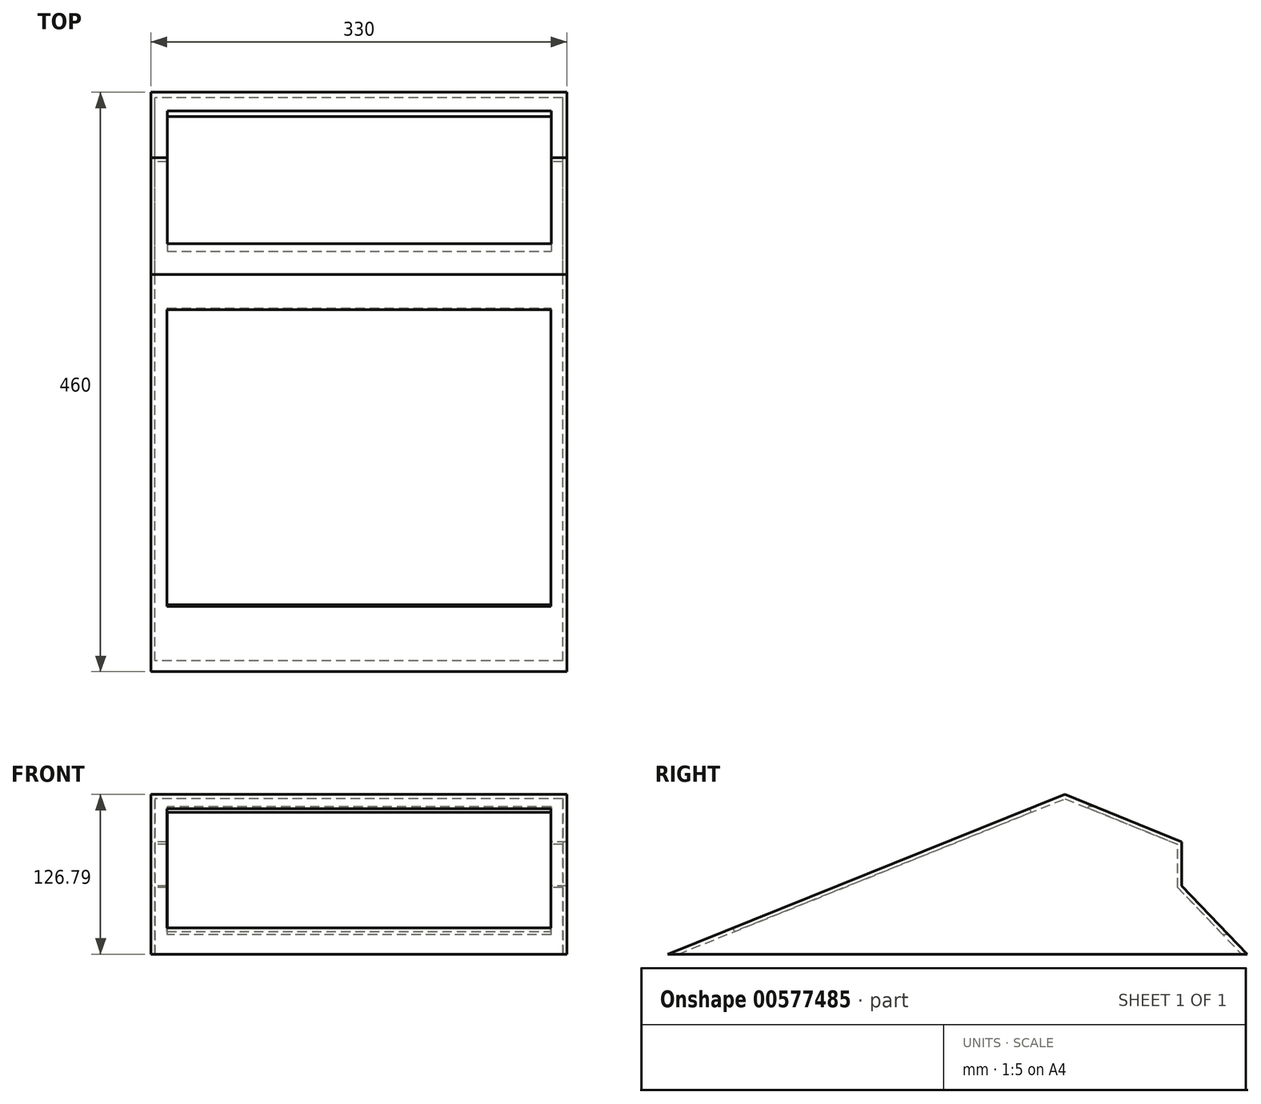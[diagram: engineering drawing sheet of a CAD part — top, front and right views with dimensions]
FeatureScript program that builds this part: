
annotation { "Feature Type Name" : "Feature", "Feature Type Description" : "" }
export const myFeature = defineFeature(function(context is Context, id is Id, definition is map)
    precondition{}
    {
        {
            var Q0;
            Q0=qCreatedBy(makeId("Right.planeOp"),FACE);
            var sketch = newSketch(context, id + "F0", { "sketchPlane" : qUnion([Q0])});
            skLineSegment(sketch, "E0", {"start": v(-333.89, 0) * mm, "end": v(-18.41, 126.79) * mm});
            skLineSegment(sketch, "E1", {"start": v(-18.41, 126.79) * mm, "end": v(74.24, 89.17) * mm});
            skLineSegment(sketch, "E2", {"start": v(74.24, 89.17) * mm, "end": v(74.24, 54.17) * mm});
            skLineSegment(sketch, "E3", {"start": v(74.24, 54.17) * mm, "end": v(126.11, 0) * mm});
            skLineSegment(sketch, "E4", {"start": v(-333.89, 0) * mm, "end": v(126.11, 0) * mm});
            skSolve(sketch);
        }
        {
            var Q0;
            Q0=makeQuery(id+"F0.imprint","IMPRINT",FACE,{"disambiguationData":[TD([[makeQuery(id+"F0.imprint","IMPRINT",EDGE,{"derivedFrom":sQuery(id+"F0.wireOp",EDGE,"E0")}),-1.0]])]});
            extrude(context, id + "F1", {"entities" : qUnion([Q0]), "depth" : 330 * mm, "offsetDistance" : 25.4 * mm});
        }
        {
            var Q0;
            Q0=makeQuery(id+"F1.opExtrude","SWEPT_FACE",FACE,{"disambiguationData":[OSD([sQuery(id+"F0.wireOp",EDGE,"E4")])]});
            shell(context, id + "F2", {"entities" : qUnion([Q0]), "thickness" : 3.17 * mm});
        }
        {
            var Q0;
            Q0=qCreatedBy(makeId("Front.planeOp"),FACE);
            var sketch = newSketch(context, id + "F3", { "sketchPlane" : qUnion([Q0])});
            skLineSegment(sketch, "E5.bottom", {"start": v(12.79, 116.98) * mm, "end": v(317.59, 116.98) * mm});
            skLineSegment(sketch, "E5.top", {"start": v(12.79, 15.38) * mm, "end": v(317.59, 15.38) * mm});
            skLineSegment(sketch, "E5.left", {"start": v(12.79, 116.98) * mm, "end": v(12.79, 15.38) * mm});
            skLineSegment(sketch, "E5.right", {"start": v(317.59, 116.98) * mm, "end": v(317.59, 15.38) * mm});
            skSolve(sketch);
        }
        {
            var Q0;
            Q0=qSketchRegion(id+"F3",true);
            extrude(context, id + "F4", {"entities" : qUnion([Q0]), "operationType" : NewBodyOperationType.REMOVE, "oppositeDirection" : true, "depth" : 254 * mm, "offsetDistance" : 25.4 * mm});
        }
        {
            var Q0;
            Q0=makeQuery(id+"F1.opExtrude","SWEPT_FACE",FACE,{"disambiguationData":[OSD([sQuery(id+"F0.wireOp",EDGE,"E0")])]});
            var sketch = newSketch(context, id + "F5", { "sketchPlane" : qUnion([Q0])});
            skLineSegment(sketch, "E6.bottom", {"start": v(12.7, 0) * mm, "end": v(317.5, 0) * mm});
            skLineSegment(sketch, "E6.top", {"start": v(12.7, -254) * mm, "end": v(317.5, -254) * mm});
            skLineSegment(sketch, "E6.left", {"start": v(12.7, 0) * mm, "end": v(12.7, -254) * mm});
            skLineSegment(sketch, "E6.right", {"start": v(317.5, 0) * mm, "end": v(317.5, -254) * mm});
            skSolve(sketch);
        }
        {
            var Q0;
            Q0=qSketchRegion(id+"F5",true);
            extrude(context, id + "F6", {"entities" : qUnion([Q0]), "operationType" : NewBodyOperationType.REMOVE, "oppositeDirection" : true, "depth" : 25.4 * mm, "offsetDistance" : 25.4 * mm});
        }
    });
